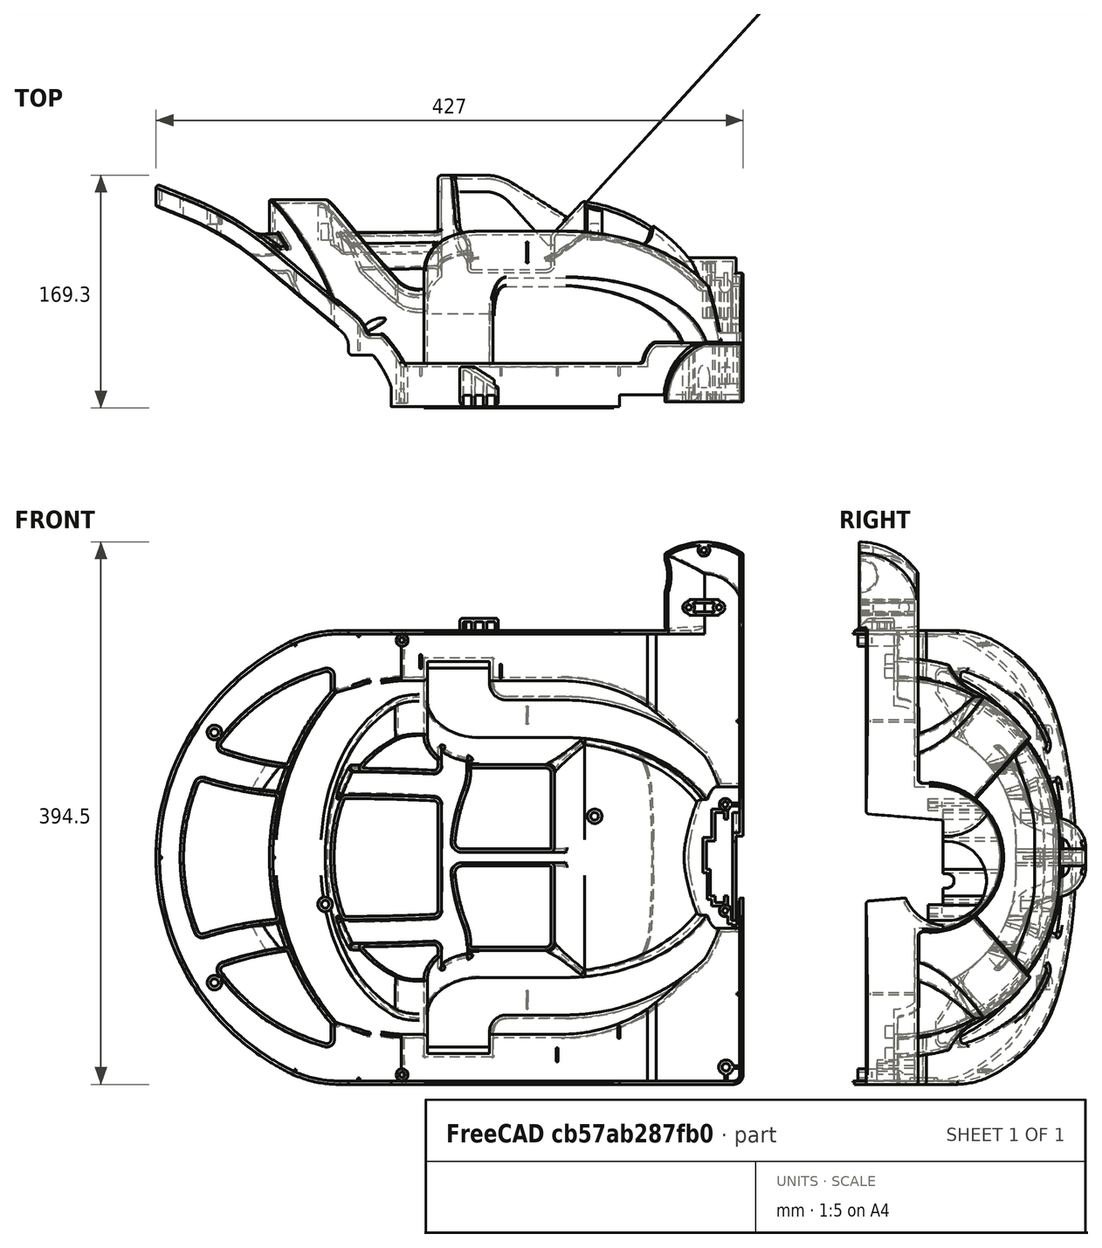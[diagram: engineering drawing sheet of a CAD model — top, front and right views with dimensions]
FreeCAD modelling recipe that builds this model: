
FCSTD DOCUMENT  (FreeCAD 0.19R24291 (Git))
Label: mask
License: All rights reserved
LicenseURL: http://en.wikipedia.org/wiki/All_rights_reserved
objects: Sketcher::SketchObject×5, Part::Feature×2, Mesh::Feature×1, PartDesign::Body×1, Part::FeaturePython×1, App::Part×1
note: 9 computed .brp shape members not serialized (recipe doc carries the construction recipe); baked Part::Feature solids carry a one-line shape summary decoded from their .brp

FEATURE [Sketcher::SketchObject] Sketch001
  AttachmentOffset = pos=(0,0,-20) rot=(0,0,1;0rad)
  FullyConstrained = true
  MapMode = 5
  Placement = pos=(-20,4.4e-15,-4.4e-15) rot=(0.57735,0.57735,0.57735;2.0944rad)
  Support = -> [YZ_Plane]
  sketch-geometry (2):
    g0: ArcOfCircle CenterX=-1.2e-15 CenterY=140 CenterZ=0 NormalX=0 NormalY=0 NormalZ=1 AngleXU=0 Radius=250 StartAngle=4.42859 EndAngle=4.99618
    g1: GeomPoint X=0 Y=-110 Z=0
  constraints (6):
    c: Symmetric(g0,g0,g-2)
    c: PointOnObject(g1,g0)
    c: PointOnObject(g1,g-2)
    c: DistanceY(g1,g-1) = 110
    c: DistanceX(g0,g0) = 140
    c: DistanceY(g0,g-1) = 100
FEATURE [Sketcher::SketchObject] Sketch
  ExternalGeometry = -> [Sketch001]
  FullyConstrained = true
  MapMode = 5
  Placement = pos=(0,0,0) rot=(1,0,0;1.5708rad)
  Support = -> [XZ_Plane]
  sketch-geometry (1):
    g0: ArcOfCircle CenterX=0 CenterY=0 CenterZ=0 NormalX=0 NormalY=0 NormalZ=1 AngleXU=0 Radius=111.803 StartAngle=3.77674 EndAngle=4.53254
  constraints (4):
    c: Coincident(g0,g-1)
    c: DistanceX(g0,g-1) = 20
    c: DistanceX(g0,g-1) = 90
    c: DistanceY(g0,g-1) = 110
FEATURE [Mesh::Feature] fhlin
  Placement = pos=(40,0,30) rot=(0,0,1;1.5708rad)
FEATURE [Sketcher::SketchObject] Sketch002
  AttachmentOffset = pos=(0,0,-66.33) rot=(0,0,1;0rad)
  ExternalGeometry = -> [Sketch]
  FullyConstrained = false
  MapMode = 5
  Placement = pos=(0,0,-66.33) rot=(0,0,1;0rad)
  Support = -> [XY_Plane]
  sketch-geometry (2):
    g0: ArcOfCircle CenterX=-5.15799 CenterY=-1.5e-15 CenterZ=0 NormalX=0 NormalY=0 NormalZ=1 AngleXU=0 Radius=84.842 StartAngle=2.17128 EndAngle=4.11191
    g1: GeomPoint X=-90 Y=0 Z=0
  constraints (5):
    c: Symmetric(g0,g0,g-1)
    c: PointOnObject(g1,g0)
    c: PointOnObject(g1,g-1)
    c: DistanceX(g1,g-1) = 90
    c: DistanceY(g0,g0) = 140
FEATURE [Sketcher::SketchObject] Sketch003
  AttachmentOffset = pos=(0,0,70) rot=(0,0,1;0rad)
  ExternalGeometry = -> [Sketch002,Sketch001]
  FullyConstrained = true
  MapMode = 5
  Placement = pos=(0,-70,-1.55e-14) rot=(1,0,0;1.5708rad)
  Support = -> [XZ_Plane]
  sketch-geometry (1):
    g0: ArcOfCircle CenterX=0 CenterY=-47.2382 CenterZ=0 NormalX=0 NormalY=0 NormalZ=1 AngleXU=0 Radius=56.4253 StartAngle=3.48676 EndAngle=4.35006
  constraints (3):
    c: Coincident(g0,g-3)
    c: Coincident(g0,g-4)
    c: PointOnObject(g0,g-2)
FEATURE [Sketcher::SketchObject] Sketch004
  AttachmentOffset = pos=(0,0,-70) rot=(0,0,1;0rad)
  ExternalGeometry = -> [Sketch002,Sketch003]
  FullyConstrained = true
  MapMode = 5
  Placement = pos=(0,70,1.55e-14) rot=(1,0,0;1.5708rad)
  Support = -> [XZ_Plane]
  sketch-geometry (1):
    g0: ArcOfCircle CenterX=0 CenterY=-47.2382 CenterZ=0 NormalX=0 NormalY=0 NormalZ=1 AngleXU=0 Radius=56.4253 StartAngle=3.48676 EndAngle=4.35006
  constraints (3):
    c: Coincident(g0,g-4)
    c: Coincident(g0,g-4)
    c: PointOnObject(g0,g-2)
FEATURE [PartDesign::Body] Body
  Group = -> [Sketch,Sketch001,Sketch002,Sketch003,Sketch004]
  Origin = -> Origin
FEATURE [Part::FeaturePython] CurvedArray  # WARN: FeaturePython — macro-defined, semantics opaque (R4)
  Axis = (0,1,0)
  Base = -> Sketch
  Distribution = 0
  DistributionReverse = false
  Hullcurves = -> [Sketch001,Sketch002,Sketch003,Sketch004]
  Items = 50
  OffsetEnd = 0
  OffsetStart = 0
  Solid = false
  Surface = true
  Twist = 0
FEATURE [Part::Feature] Part__Feature  label="SOLID"
  shape: bbox 534.1 x 266.3 x 472.1 mm, 1391 faces (baked)
FEATURE [Part::Feature] Part__Feature001  label="COMPOUND"
  shape: bbox 86.96 x 50.2 x 2e-07 mm, 0 faces, 0 solids (baked)
FEATURE [App::Part] Verkleidung_64_OT
  Group = -> [Part__Feature,Part__Feature001]
  Origin = -> Origin001
  Placement = pos=(98.6233,-500,381.372) rot=(-0.610924,0.559809,-0.559809;4.23842rad)
